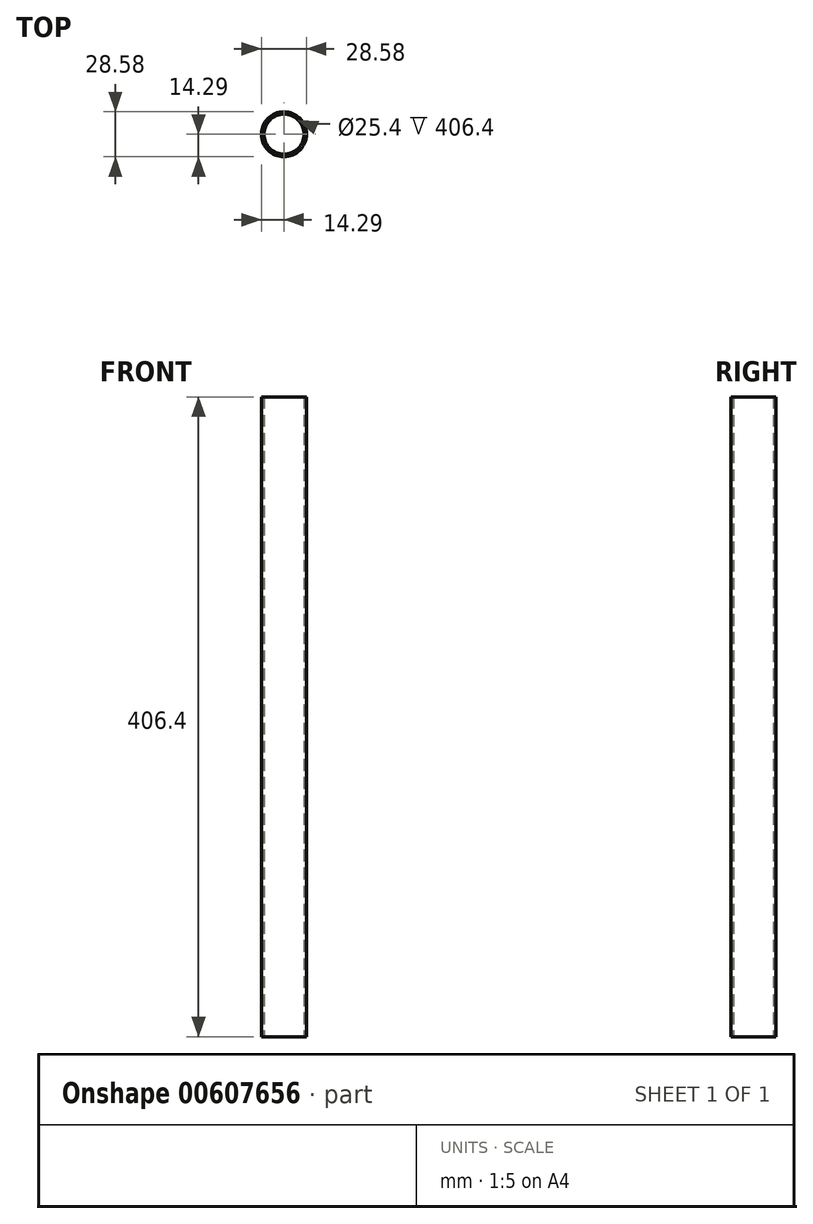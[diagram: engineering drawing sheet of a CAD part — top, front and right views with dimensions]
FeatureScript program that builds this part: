
annotation { "Feature Type Name" : "Feature", "Feature Type Description" : "" }
export const myFeature = defineFeature(function(context is Context, id is Id, definition is map)
    precondition{}
    {
        {
            var Q0;
            Q0=qCreatedBy(makeId("Top.planeOp"),FACE);
            var sketch = newSketch(context, id + "F0", { "sketchPlane" : qUnion([Q0])});
            skLineSegment(sketch, "E0", {"start": v(0, 0) * mm, "end": v(12.7, 0) * mm});
            skCircle(sketch, "E1", {"center": v(0, 0) * mm, "radius": 12.7 * mm});
            skCircle(sketch, "E2.0", {"center": v(0, 0) * mm, "radius": 14.29 * mm});
            skSolve(sketch);
        }
        {
            var Q0;
            Q0=qSketchRegion(id+"FEloJnSHgHgsXCt_0",true);
            var Q1;
            Q1=makeQuery(id+"F0.imprint","IMPRINT",FACE,{"disambiguationData":[TD([[makeQuery(id+"F0.imprint","IMPRINT",EDGE,{"derivedFrom":sQuery(id+"F0.wireOp",EDGE,"E1")}),-1.0]])]});
            extrude(context, id + "F1", {"entities" : qUnion([Q0, Q1]), "depth" : 406.4 * mm, "offsetDistance" : 25.4 * mm});
        }
    });
